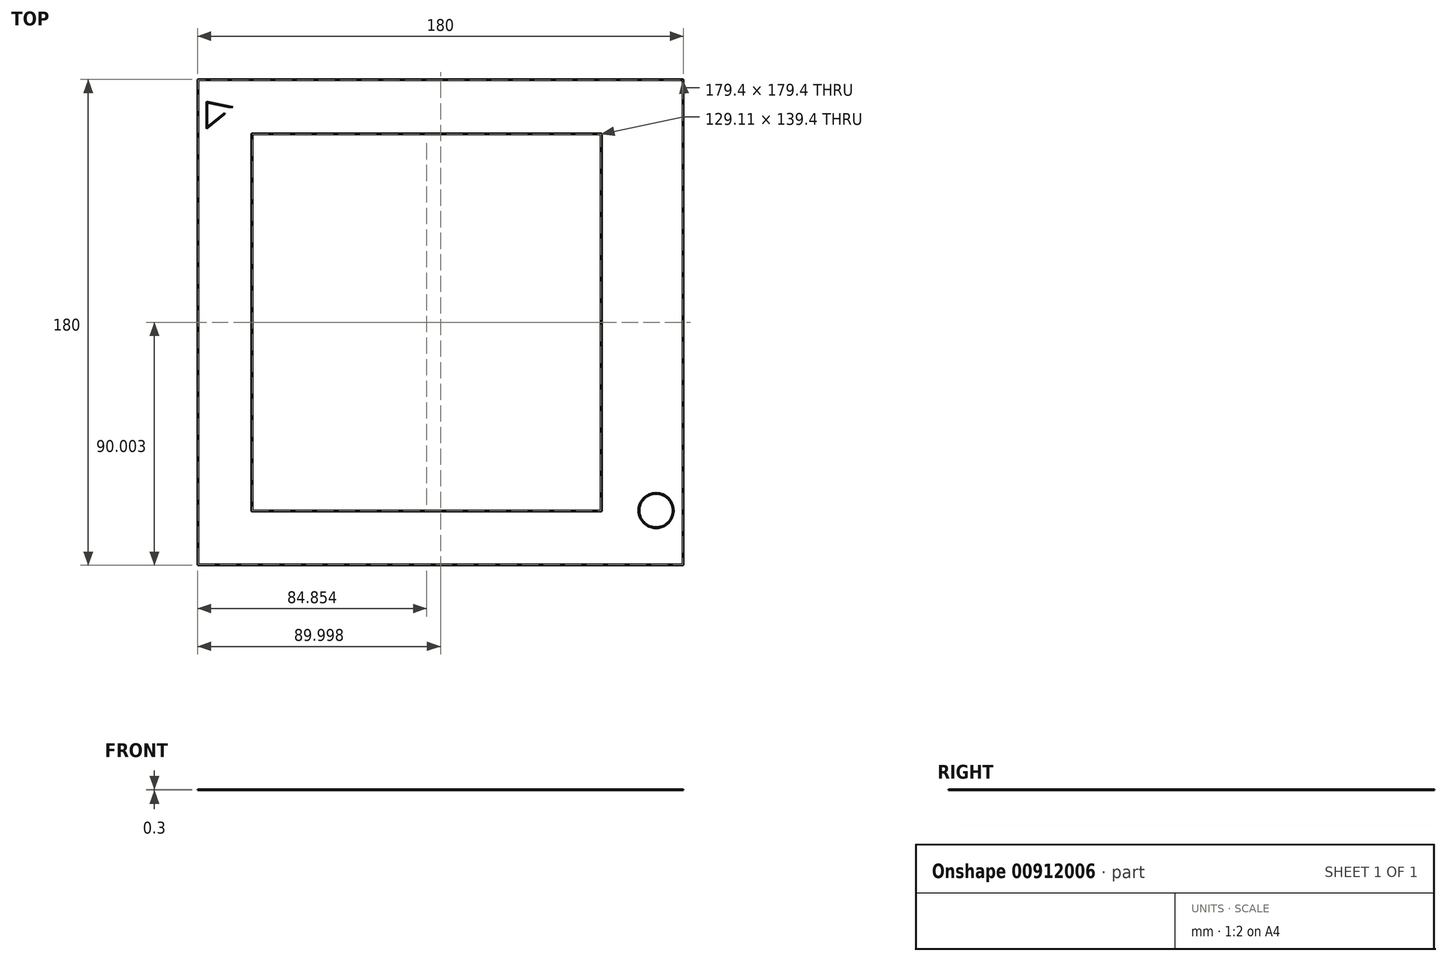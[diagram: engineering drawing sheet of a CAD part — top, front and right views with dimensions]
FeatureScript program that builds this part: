
annotation { "Feature Type Name" : "Feature", "Feature Type Description" : "" }
export const myFeature = defineFeature(function(context is Context, id is Id, definition is map)
    precondition{}
    {
        {
            assignVariable(context, id + "F0", {"name" : "LineHeight", "anyValue" : 0.3});
        }
        {
            var Q0;
            Q0=qCreatedBy(makeId("Top.planeOp"),FACE);
            var sketch = newSketch(context, id + "F1", { "sketchPlane" : qUnion([Q0])});
            skLineSegment(sketch, "E0.bottom", {"start": v(-91.48, 107.86) * mm, "end": v(88.52, 107.86) * mm});
            skLineSegment(sketch, "E0.top", {"start": v(-91.48, -72.14) * mm, "end": v(88.52, -72.14) * mm});
            skLineSegment(sketch, "E0.left", {"start": v(-91.48, 107.86) * mm, "end": v(-91.48, -72.14) * mm});
            skLineSegment(sketch, "E0.right", {"start": v(88.52, 107.86) * mm, "end": v(88.52, -72.14) * mm});
            skLineSegment(sketch, "E1.bottom", {"start": v(-81.48, 97.86) * mm, "end": v(68.23, 97.86) * mm});
            skLineSegment(sketch, "E1.top", {"start": v(-81.48, -62.14) * mm, "end": v(68.23, -62.14) * mm});
            skLineSegment(sketch, "E1.left", {"start": v(-81.48, 97.86) * mm, "end": v(-81.48, -62.14) * mm});
            skLineSegment(sketch, "E1.right", {"start": v(68.23, 97.86) * mm, "end": v(68.23, -62.14) * mm});
            skLineSegment(sketch, "E2.bottom", {"start": v(-71.48, 87.86) * mm, "end": v(58.23, 87.86) * mm});
            skLineSegment(sketch, "E2.top", {"start": v(-71.48, -52.14) * mm, "end": v(58.23, -52.14) * mm});
            skLineSegment(sketch, "E2.left", {"start": v(-71.48, 87.86) * mm, "end": v(-71.48, -52.14) * mm});
            skLineSegment(sketch, "E2.right", {"start": v(58.23, 87.86) * mm, "end": v(58.23, -52.14) * mm});
            skLineSegment(sketch, "E3.bottom", {"start": v(-41.48, 57.86) * mm, "end": v(38.52, 57.86) * mm});
            skLineSegment(sketch, "E3.top", {"start": v(-41.48, -22.14) * mm, "end": v(38.52, -22.14) * mm});
            skLineSegment(sketch, "E3.left", {"start": v(-41.48, 57.86) * mm, "end": v(-41.48, -22.14) * mm});
            skLineSegment(sketch, "E3.right", {"start": v(38.52, 57.86) * mm, "end": v(38.52, -22.14) * mm});
            skLineSegment(sketch, "E4", {"start": v(-88.18, 99.56) * mm, "end": v(-88.18, 89.56) * mm});
            skLineSegment(sketch, "E5", {"start": v(-88.18, 89.56) * mm, "end": v(-78.38, 97.56) * mm});
            skLineSegment(sketch, "E6", {"start": v(-78.38, 97.56) * mm, "end": v(-88.18, 99.56) * mm});
            skCircle(sketch, "E7", {"center": v(78.37, -51.84) * mm, "radius": 6.5 * mm});
            skLineSegment(sketch, "E8", {"start": v(68.23, -51.84) * mm, "end": v(88.52, -51.84) * mm, "construction": true});
            skLineSegment(sketch, "E9", {"start": v(-91.18, 107.56) * mm, "end": v(88.22, 107.56) * mm});
            skLineSegment(sketch, "E10", {"start": v(88.22, 107.56) * mm, "end": v(88.22, -71.84) * mm});
            skLineSegment(sketch, "E11", {"start": v(88.22, -71.84) * mm, "end": v(-91.18, -71.84) * mm});
            skLineSegment(sketch, "E12", {"start": v(-91.18, -71.84) * mm, "end": v(-91.18, 107.56) * mm});
            skLineSegment(sketch, "E13", {"start": v(-81.18, 97.56) * mm, "end": v(67.93, 97.56) * mm});
            skLineSegment(sketch, "E14", {"start": v(67.93, 97.56) * mm, "end": v(67.93, -61.84) * mm});
            skLineSegment(sketch, "E15", {"start": v(67.93, -61.84) * mm, "end": v(-81.18, -61.84) * mm});
            skLineSegment(sketch, "E16", {"start": v(-81.18, -61.84) * mm, "end": v(-81.18, 97.56) * mm});
            skLineSegment(sketch, "E17", {"start": v(-71.18, 87.56) * mm, "end": v(57.93, 87.56) * mm});
            skLineSegment(sketch, "E18", {"start": v(57.93, 87.56) * mm, "end": v(57.93, -51.84) * mm});
            skLineSegment(sketch, "E19", {"start": v(57.93, -51.84) * mm, "end": v(-71.18, -51.84) * mm});
            skLineSegment(sketch, "E20", {"start": v(-71.18, -51.84) * mm, "end": v(-71.18, 87.56) * mm});
            skCircle(sketch, "E21", {"center": v(78.37, -51.84) * mm, "radius": 6.2 * mm});
            skLineSegment(sketch, "E22", {"start": v(-87.88, 99.2) * mm, "end": v(-79.06, 97.4) * mm});
            skPoint(sketch, "E22.startSnap0", {"position": v(-85.81, 99.2) * mm});
            skLineSegment(sketch, "E23", {"start": v(-79.06, 97.4) * mm, "end": v(-87.88, 90.2) * mm});
            skLineSegment(sketch, "E24", {"start": v(-87.88, 90.2) * mm, "end": v(-87.88, 99.2) * mm});
            skSolve(sketch);
        }
        {
            var Q0;
            Q0=makeQuery(id+"F1.imprint","IMPRINT",FACE,{"disambiguationData":[TD([[makeQuery(id+"F1.imprint","IMPRINT",EDGE,{"derivedFrom":sQuery(id+"F1.wireOp",EDGE,"E0.bottom")}),-1.0]])]});
            var Q1;
            Q1=makeQuery(id+"F1.imprint","IMPRINT",FACE,{"disambiguationData":[TD([[makeQuery(id+"F1.imprint","IMPRINT",EDGE,{"derivedFrom":sQuery(id+"F1.wireOp",EDGE,"E1.bottom")}),-1.0]])]});
            var Q2;
            Q2=makeQuery(id+"F1.imprint","IMPRINT",FACE,{"disambiguationData":[TD([[makeQuery(id+"F1.imprint","IMPRINT",EDGE,{"derivedFrom":sQuery(id+"F1.wireOp",EDGE,"E2.bottom")}),-1.0]])]});
            var Q3;
            Q3=makeQuery(id+"F1.imprint","IMPRINT",FACE,{"disambiguationData":[TD([[makeQuery(id+"F1.imprint","IMPRINT",EDGE,{"derivedFrom":sQuery(id+"F1.wireOp",EDGE,"E7")}),1.0]])]});
            var Q4;
            Q4=makeQuery(id+"F1.imprint","IMPRINT",FACE,{"disambiguationData":[TD([[makeQuery(id+"F1.imprint","IMPRINT",EDGE,{"derivedFrom":sQuery(id+"F1.wireOp",EDGE,"E3.bottom")}),-1.0]])]});
            var Q5;
            Q5=makeQuery(id+"F1.imprint","IMPRINT",FACE,{"disambiguationData":[TD([[makeQuery(id+"F1.imprint","IMPRINT",EDGE,{"derivedFrom":sQuery(id+"F1.wireOp",EDGE,"E4")}),1.0]])]});
            extrude(context, id + "F2", {"entities" : qUnion([Q0, Q1, Q2, Q3, Q4, Q5]), "depth" : (getVariable(context, 'LineHeight')) * mm, "offsetDistance" : 25 * mm});
        }
        {
            var Q0;
            Q0=makeQuery(id+"F2.opExtrude","SWEPT_BODY",BODY,{"disambiguationData":[OSD([sQuery(id+"F1.wireOp",EDGE,"E3.bottom"),sQuery(id+"F1.wireOp",EDGE,"E3.top"),sQuery(id+"F1.wireOp",EDGE,"E3.left"),sQuery(id+"F1.wireOp",EDGE,"E3.right")])]});
            deleteBodies(context, id + "F3", {"entities" : qUnion([Q0])});
        }
    });
